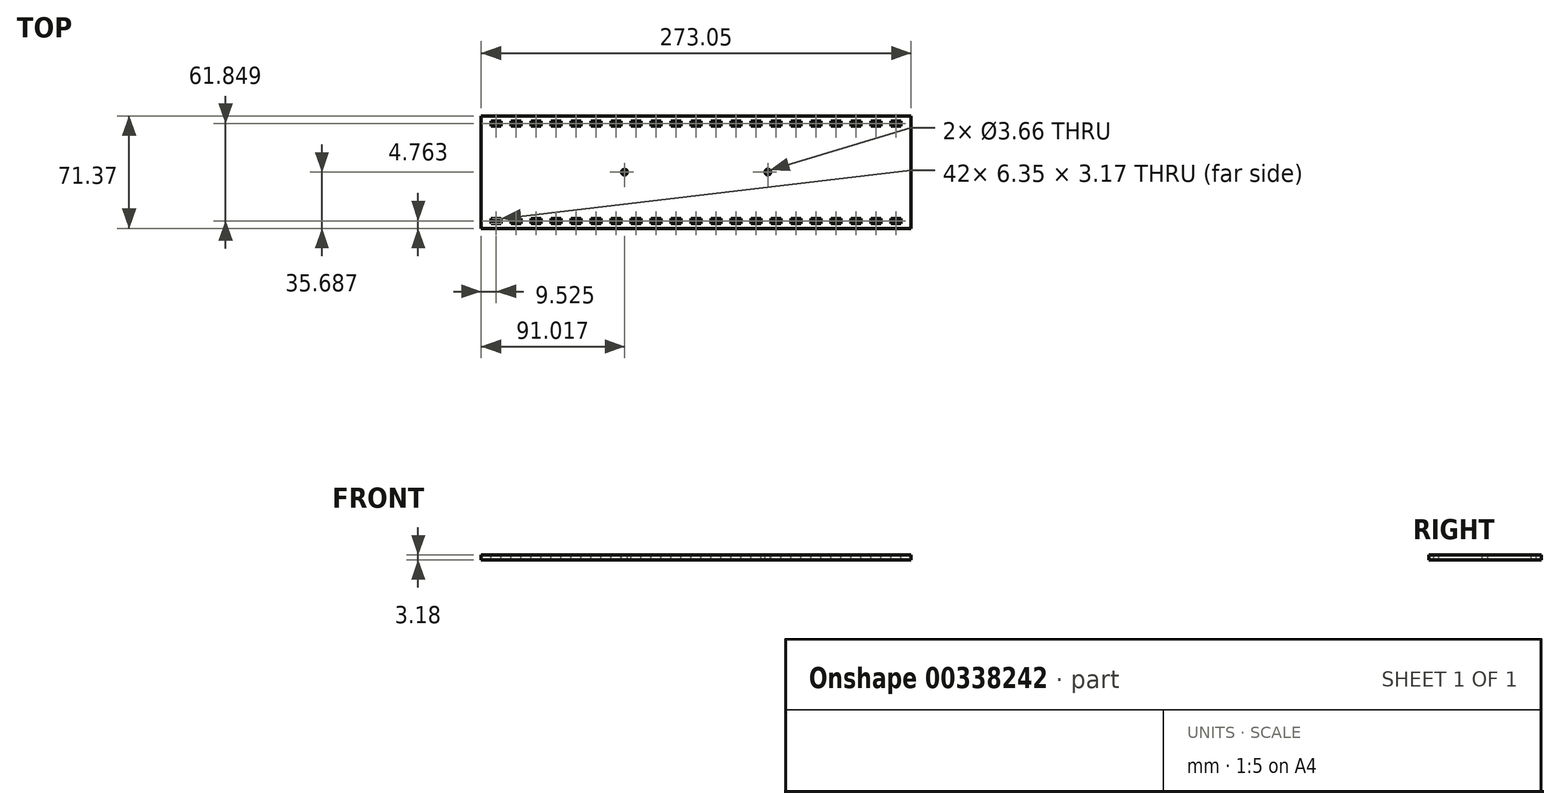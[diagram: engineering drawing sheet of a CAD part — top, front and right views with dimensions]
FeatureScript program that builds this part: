
annotation { "Feature Type Name" : "Feature", "Feature Type Description" : "" }
export const myFeature = defineFeature(function(context is Context, id is Id, definition is map)
    precondition{}
    {
        {
            var Q0;
            Q0=qCreatedBy(makeId("Top.planeOp"),FACE);
            var sketch = newSketch(context, id + "F0", { "sketchPlane" : qUnion([Q0])});
            skLineSegment(sketch, "E0.bottom", {"start": v(0, 0) * mm, "end": v(-273.05, 0) * mm});
            skLineSegment(sketch, "E0.top", {"start": v(0, 71.37) * mm, "end": v(-273.05, 71.37) * mm});
            skLineSegment(sketch, "E0.left", {"start": v(0, 0) * mm, "end": v(0, 71.37) * mm});
            skLineSegment(sketch, "E0.right", {"start": v(-273.05, 0) * mm, "end": v(-273.05, 71.37) * mm});
            skSolve(sketch);
        }
        {
            var Q0;
            Q0=qSketchRegion(id+"F0",true);
            extrude(context, id + "F1", {"entities" : qUnion([Q0]), "depth" : 3.17 * mm});
        }
        {
            var Q0;
            Q0=makeQuery(id+"F1.opExtrude","CAP_FACE",FACE,{"disambiguationData":[OSD([sQuery(id+"F0.wireOp",EDGE,"E0.bottom"),sQuery(id+"F0.wireOp",EDGE,"E0.top"),sQuery(id+"F0.wireOp",EDGE,"E0.left"),sQuery(id+"F0.wireOp",EDGE,"E0.right")])],"isStart":false});
            var sketch = newSketch(context, id + "F2", { "sketchPlane" : qUnion([Q0])});
            skLineSegment(sketch, "E1", {"start": v(0, 4.76) * mm, "end": v(-6.35, 4.76) * mm, "construction": true});
            skLineSegment(sketch, "E2", {"start": v(0, 35.69) * mm, "end": v(-91.02, 35.69) * mm, "construction": true});
            skLineSegment(sketch, "E3", {"start": v(-91.02, 35.69) * mm, "end": v(-182.03, 35.69) * mm, "construction": true});
            skLineSegment(sketch, "E4", {"start": v(-182.03, 35.69) * mm, "end": v(-273.05, 35.69) * mm, "construction": true});
            skCircle(sketch, "E5", {"center": v(-182.03, 35.69) * mm, "radius": 1.83 * mm});
            skCircle(sketch, "E6", {"center": v(-91.02, 35.69) * mm, "radius": 1.83 * mm});
            skLineSegment(sketch, "E7.bottom", {"start": v(-6.35, 3.18) * mm, "end": v(-12.7, 3.17) * mm});
            skLineSegment(sketch, "E7.top", {"start": v(-6.35, 6.35) * mm, "end": v(-12.7, 6.35) * mm});
            skLineSegment(sketch, "E7.left", {"start": v(-6.35, 3.17) * mm, "end": v(-6.35, 6.35) * mm});
            skLineSegment(sketch, "E7.right", {"start": v(-12.7, 3.18) * mm, "end": v(-12.7, 6.35) * mm});
            skLineSegment(sketch, "E8", {"start": v(-9.53, 3.18) * mm, "end": v(-9.53, 0) * mm, "construction": true});
            skLineSegment(sketch, "E9", {"start": v(-9.53, 71.37) * mm, "end": v(-9.53, 68.2) * mm, "construction": true});
            skLineSegment(sketch, "E10.bottom", {"start": v(-12.7, 68.2) * mm, "end": v(-6.35, 68.2) * mm});
            skLineSegment(sketch, "E10.top", {"start": v(-12.7, 65.02) * mm, "end": v(-6.35, 65.02) * mm});
            skLineSegment(sketch, "E10.left", {"start": v(-12.7, 68.2) * mm, "end": v(-12.7, 65.02) * mm});
            skLineSegment(sketch, "E10.right", {"start": v(-6.35, 68.2) * mm, "end": v(-6.35, 65.02) * mm});
            skLineSegment(sketch, "E11", {"start": v(-6.35, 66.61) * mm, "end": v(0, 66.61) * mm, "construction": true});
            skLineSegment(sketch, "E12.1.0.0", {"start": v(-19.05, 66.61) * mm, "end": v(-12.7, 66.61) * mm, "construction": true});
            skLineSegment(sketch, "E12.1.0.1", {"start": v(-25.4, 68.2) * mm, "end": v(-19.05, 68.2) * mm});
            skLineSegment(sketch, "E12.1.0.2", {"start": v(-25.4, 68.2) * mm, "end": v(-25.4, 65.02) * mm});
            skLineSegment(sketch, "E12.1.0.3", {"start": v(-25.4, 65.02) * mm, "end": v(-19.05, 65.02) * mm});
            skLineSegment(sketch, "E12.1.0.4", {"start": v(-19.05, 68.2) * mm, "end": v(-19.05, 65.02) * mm});
            skLineSegment(sketch, "E12.2.0.0", {"start": v(-31.75, 66.61) * mm, "end": v(-25.4, 66.61) * mm, "construction": true});
            skLineSegment(sketch, "E12.2.0.1", {"start": v(-38.1, 68.2) * mm, "end": v(-31.75, 68.2) * mm});
            skLineSegment(sketch, "E12.2.0.2", {"start": v(-38.1, 68.2) * mm, "end": v(-38.1, 65.02) * mm});
            skLineSegment(sketch, "E12.2.0.3", {"start": v(-38.1, 65.02) * mm, "end": v(-31.75, 65.02) * mm});
            skLineSegment(sketch, "E12.2.0.4", {"start": v(-31.75, 68.2) * mm, "end": v(-31.75, 65.02) * mm});
            skLineSegment(sketch, "E12.3.0.0", {"start": v(-44.45, 66.61) * mm, "end": v(-38.1, 66.61) * mm, "construction": true});
            skLineSegment(sketch, "E12.3.0.1", {"start": v(-50.8, 68.2) * mm, "end": v(-44.45, 68.2) * mm});
            skLineSegment(sketch, "E12.3.0.2", {"start": v(-50.8, 68.2) * mm, "end": v(-50.8, 65.02) * mm});
            skLineSegment(sketch, "E12.3.0.3", {"start": v(-50.8, 65.02) * mm, "end": v(-44.45, 65.02) * mm});
            skLineSegment(sketch, "E12.3.0.4", {"start": v(-44.45, 68.2) * mm, "end": v(-44.45, 65.02) * mm});
            skLineSegment(sketch, "E12.4.0.0", {"start": v(-57.15, 66.61) * mm, "end": v(-50.8, 66.61) * mm, "construction": true});
            skLineSegment(sketch, "E12.4.0.1", {"start": v(-63.5, 68.2) * mm, "end": v(-57.15, 68.2) * mm});
            skLineSegment(sketch, "E12.4.0.2", {"start": v(-63.5, 68.2) * mm, "end": v(-63.5, 65.02) * mm});
            skLineSegment(sketch, "E12.4.0.3", {"start": v(-63.5, 65.02) * mm, "end": v(-57.15, 65.02) * mm});
            skLineSegment(sketch, "E12.4.0.4", {"start": v(-57.15, 68.2) * mm, "end": v(-57.15, 65.02) * mm});
            skLineSegment(sketch, "E12.5.0.0", {"start": v(-69.85, 66.61) * mm, "end": v(-63.5, 66.61) * mm, "construction": true});
            skLineSegment(sketch, "E12.5.0.1", {"start": v(-76.2, 68.2) * mm, "end": v(-69.85, 68.2) * mm});
            skLineSegment(sketch, "E12.5.0.2", {"start": v(-76.2, 68.2) * mm, "end": v(-76.2, 65.02) * mm});
            skLineSegment(sketch, "E12.5.0.3", {"start": v(-76.2, 65.02) * mm, "end": v(-69.85, 65.02) * mm});
            skLineSegment(sketch, "E12.5.0.4", {"start": v(-69.85, 68.2) * mm, "end": v(-69.85, 65.02) * mm});
            skLineSegment(sketch, "E12.6.0.0", {"start": v(-82.55, 66.61) * mm, "end": v(-76.2, 66.61) * mm, "construction": true});
            skLineSegment(sketch, "E12.6.0.1", {"start": v(-88.9, 68.2) * mm, "end": v(-82.55, 68.2) * mm});
            skLineSegment(sketch, "E12.6.0.2", {"start": v(-88.9, 68.2) * mm, "end": v(-88.9, 65.02) * mm});
            skLineSegment(sketch, "E12.6.0.3", {"start": v(-88.9, 65.02) * mm, "end": v(-82.55, 65.02) * mm});
            skLineSegment(sketch, "E12.6.0.4", {"start": v(-82.55, 68.2) * mm, "end": v(-82.55, 65.02) * mm});
            skLineSegment(sketch, "E12.7.0.0", {"start": v(-95.25, 66.61) * mm, "end": v(-88.9, 66.61) * mm, "construction": true});
            skLineSegment(sketch, "E12.7.0.1", {"start": v(-101.6, 68.2) * mm, "end": v(-95.25, 68.2) * mm});
            skLineSegment(sketch, "E12.7.0.2", {"start": v(-101.6, 68.2) * mm, "end": v(-101.6, 65.02) * mm});
            skLineSegment(sketch, "E12.7.0.3", {"start": v(-101.6, 65.02) * mm, "end": v(-95.25, 65.02) * mm});
            skLineSegment(sketch, "E12.7.0.4", {"start": v(-95.25, 68.2) * mm, "end": v(-95.25, 65.02) * mm});
            skLineSegment(sketch, "E12.8.0.0", {"start": v(-107.95, 66.61) * mm, "end": v(-101.6, 66.61) * mm, "construction": true});
            skLineSegment(sketch, "E12.8.0.1", {"start": v(-114.3, 68.2) * mm, "end": v(-107.95, 68.2) * mm});
            skLineSegment(sketch, "E12.8.0.2", {"start": v(-114.3, 68.2) * mm, "end": v(-114.3, 65.02) * mm});
            skLineSegment(sketch, "E12.8.0.3", {"start": v(-114.3, 65.02) * mm, "end": v(-107.95, 65.02) * mm});
            skLineSegment(sketch, "E12.8.0.4", {"start": v(-107.95, 68.2) * mm, "end": v(-107.95, 65.02) * mm});
            skLineSegment(sketch, "E12.9.0.0", {"start": v(-120.65, 66.61) * mm, "end": v(-114.3, 66.61) * mm, "construction": true});
            skLineSegment(sketch, "E12.9.0.1", {"start": v(-127, 68.2) * mm, "end": v(-120.65, 68.2) * mm});
            skLineSegment(sketch, "E12.9.0.2", {"start": v(-127, 68.2) * mm, "end": v(-127, 65.02) * mm});
            skLineSegment(sketch, "E12.9.0.3", {"start": v(-127, 65.02) * mm, "end": v(-120.65, 65.02) * mm});
            skLineSegment(sketch, "E12.9.0.4", {"start": v(-120.65, 68.2) * mm, "end": v(-120.65, 65.02) * mm});
            skLineSegment(sketch, "E12.10.0.0", {"start": v(-133.35, 66.61) * mm, "end": v(-127, 66.61) * mm, "construction": true});
            skLineSegment(sketch, "E12.10.0.1", {"start": v(-139.7, 68.2) * mm, "end": v(-133.35, 68.2) * mm});
            skLineSegment(sketch, "E12.10.0.2", {"start": v(-139.7, 68.2) * mm, "end": v(-139.7, 65.02) * mm});
            skLineSegment(sketch, "E12.10.0.3", {"start": v(-139.7, 65.02) * mm, "end": v(-133.35, 65.02) * mm});
            skLineSegment(sketch, "E12.10.0.4", {"start": v(-133.35, 68.2) * mm, "end": v(-133.35, 65.02) * mm});
            skLineSegment(sketch, "E12.11.0.0", {"start": v(-146.05, 66.61) * mm, "end": v(-139.7, 66.61) * mm, "construction": true});
            skLineSegment(sketch, "E12.11.0.1", {"start": v(-152.4, 68.2) * mm, "end": v(-146.05, 68.2) * mm});
            skLineSegment(sketch, "E12.11.0.2", {"start": v(-152.4, 68.2) * mm, "end": v(-152.4, 65.02) * mm});
            skLineSegment(sketch, "E12.11.0.3", {"start": v(-152.4, 65.02) * mm, "end": v(-146.05, 65.02) * mm});
            skLineSegment(sketch, "E12.11.0.4", {"start": v(-146.05, 68.2) * mm, "end": v(-146.05, 65.02) * mm});
            skLineSegment(sketch, "E12.12.0.0", {"start": v(-158.75, 66.61) * mm, "end": v(-152.4, 66.61) * mm, "construction": true});
            skLineSegment(sketch, "E12.12.0.1", {"start": v(-165.1, 68.2) * mm, "end": v(-158.75, 68.2) * mm});
            skLineSegment(sketch, "E12.12.0.2", {"start": v(-165.1, 68.2) * mm, "end": v(-165.1, 65.02) * mm});
            skLineSegment(sketch, "E12.12.0.3", {"start": v(-165.1, 65.02) * mm, "end": v(-158.75, 65.02) * mm});
            skLineSegment(sketch, "E12.12.0.4", {"start": v(-158.75, 68.2) * mm, "end": v(-158.75, 65.02) * mm});
            skLineSegment(sketch, "E12.13.0.0", {"start": v(-171.45, 66.61) * mm, "end": v(-165.1, 66.61) * mm, "construction": true});
            skLineSegment(sketch, "E12.13.0.1", {"start": v(-177.8, 68.2) * mm, "end": v(-171.45, 68.2) * mm});
            skLineSegment(sketch, "E12.13.0.2", {"start": v(-177.8, 68.2) * mm, "end": v(-177.8, 65.02) * mm});
            skLineSegment(sketch, "E12.13.0.3", {"start": v(-177.8, 65.02) * mm, "end": v(-171.45, 65.02) * mm});
            skLineSegment(sketch, "E12.13.0.4", {"start": v(-171.45, 68.2) * mm, "end": v(-171.45, 65.02) * mm});
            skLineSegment(sketch, "E12.14.0.0", {"start": v(-184.15, 66.61) * mm, "end": v(-177.8, 66.61) * mm, "construction": true});
            skLineSegment(sketch, "E12.14.0.1", {"start": v(-190.5, 68.2) * mm, "end": v(-184.15, 68.2) * mm});
            skLineSegment(sketch, "E12.14.0.2", {"start": v(-190.5, 68.2) * mm, "end": v(-190.5, 65.02) * mm});
            skLineSegment(sketch, "E12.14.0.3", {"start": v(-190.5, 65.02) * mm, "end": v(-184.15, 65.02) * mm});
            skLineSegment(sketch, "E12.14.0.4", {"start": v(-184.15, 68.2) * mm, "end": v(-184.15, 65.02) * mm});
            skLineSegment(sketch, "E12.15.0.0", {"start": v(-196.85, 66.61) * mm, "end": v(-190.5, 66.61) * mm, "construction": true});
            skLineSegment(sketch, "E12.15.0.1", {"start": v(-203.2, 68.2) * mm, "end": v(-196.85, 68.2) * mm});
            skLineSegment(sketch, "E12.15.0.2", {"start": v(-203.2, 68.2) * mm, "end": v(-203.2, 65.02) * mm});
            skLineSegment(sketch, "E12.15.0.3", {"start": v(-203.2, 65.02) * mm, "end": v(-196.85, 65.02) * mm});
            skLineSegment(sketch, "E12.15.0.4", {"start": v(-196.85, 68.2) * mm, "end": v(-196.85, 65.02) * mm});
            skLineSegment(sketch, "E12.16.0.0", {"start": v(-209.55, 66.61) * mm, "end": v(-203.2, 66.61) * mm, "construction": true});
            skLineSegment(sketch, "E12.16.0.1", {"start": v(-215.9, 68.2) * mm, "end": v(-209.55, 68.2) * mm});
            skLineSegment(sketch, "E12.16.0.2", {"start": v(-215.9, 68.2) * mm, "end": v(-215.9, 65.02) * mm});
            skLineSegment(sketch, "E12.16.0.3", {"start": v(-215.9, 65.02) * mm, "end": v(-209.55, 65.02) * mm});
            skLineSegment(sketch, "E12.16.0.4", {"start": v(-209.55, 68.2) * mm, "end": v(-209.55, 65.02) * mm});
            skLineSegment(sketch, "E12.17.0.0", {"start": v(-222.25, 66.61) * mm, "end": v(-215.9, 66.61) * mm, "construction": true});
            skLineSegment(sketch, "E12.17.0.1", {"start": v(-228.6, 68.2) * mm, "end": v(-222.25, 68.2) * mm});
            skLineSegment(sketch, "E12.17.0.2", {"start": v(-228.6, 68.2) * mm, "end": v(-228.6, 65.02) * mm});
            skLineSegment(sketch, "E12.17.0.3", {"start": v(-228.6, 65.02) * mm, "end": v(-222.25, 65.02) * mm});
            skLineSegment(sketch, "E12.17.0.4", {"start": v(-222.25, 68.2) * mm, "end": v(-222.25, 65.02) * mm});
            skLineSegment(sketch, "E12.18.0.0", {"start": v(-234.95, 66.61) * mm, "end": v(-228.6, 66.61) * mm, "construction": true});
            skLineSegment(sketch, "E12.18.0.1", {"start": v(-241.3, 68.2) * mm, "end": v(-234.95, 68.2) * mm});
            skLineSegment(sketch, "E12.18.0.2", {"start": v(-241.3, 68.2) * mm, "end": v(-241.3, 65.02) * mm});
            skLineSegment(sketch, "E12.18.0.3", {"start": v(-241.3, 65.02) * mm, "end": v(-234.95, 65.02) * mm});
            skLineSegment(sketch, "E12.18.0.4", {"start": v(-234.95, 68.2) * mm, "end": v(-234.95, 65.02) * mm});
            skLineSegment(sketch, "E12.19.0.0", {"start": v(-247.65, 66.61) * mm, "end": v(-241.3, 66.61) * mm, "construction": true});
            skLineSegment(sketch, "E12.19.0.1", {"start": v(-254, 68.2) * mm, "end": v(-247.65, 68.2) * mm});
            skLineSegment(sketch, "E12.19.0.2", {"start": v(-254, 68.2) * mm, "end": v(-254, 65.02) * mm});
            skLineSegment(sketch, "E12.19.0.3", {"start": v(-254, 65.02) * mm, "end": v(-247.65, 65.02) * mm});
            skLineSegment(sketch, "E12.19.0.4", {"start": v(-247.65, 68.2) * mm, "end": v(-247.65, 65.02) * mm});
            skLineSegment(sketch, "E12.20.0.0", {"start": v(-260.35, 66.61) * mm, "end": v(-254, 66.61) * mm, "construction": true});
            skLineSegment(sketch, "E12.20.0.1", {"start": v(-266.7, 68.2) * mm, "end": v(-260.35, 68.2) * mm});
            skLineSegment(sketch, "E12.20.0.2", {"start": v(-266.7, 68.2) * mm, "end": v(-266.7, 65.02) * mm});
            skLineSegment(sketch, "E12.20.0.3", {"start": v(-266.7, 65.02) * mm, "end": v(-260.35, 65.02) * mm});
            skLineSegment(sketch, "E12.20.0.4", {"start": v(-260.35, 68.2) * mm, "end": v(-260.35, 65.02) * mm});
            skLineSegment(sketch, "E12.21.0.0", {"start": v(-273.05, 66.61) * mm, "end": v(-266.7, 66.61) * mm, "construction": true});
            skLineSegment(sketch, "E12.21.0.1", {"start": v(-279.4, 68.2) * mm, "end": v(-273.05, 68.2) * mm});
            skLineSegment(sketch, "E12.21.0.2", {"start": v(-279.4, 68.2) * mm, "end": v(-279.4, 65.02) * mm});
            skLineSegment(sketch, "E12.21.0.3", {"start": v(-279.4, 65.02) * mm, "end": v(-273.05, 65.02) * mm});
            skLineSegment(sketch, "E12.21.0.4", {"start": v(-273.05, 68.2) * mm, "end": v(-273.05, 65.02) * mm});
            skLineSegment(sketch, "E12.direction1", {"start": v(-12.7, 65.02) * mm, "end": v(-25.4, 65.02) * mm, "construction": true});
            skLineSegment(sketch, "E13.1.0.0", {"start": v(-12.7, 4.76) * mm, "end": v(-19.05, 4.76) * mm, "construction": true});
            skLineSegment(sketch, "E13.1.0.1", {"start": v(-19.05, 6.35) * mm, "end": v(-25.4, 6.35) * mm});
            skLineSegment(sketch, "E13.1.0.2", {"start": v(-19.05, 3.17) * mm, "end": v(-19.05, 6.35) * mm});
            skLineSegment(sketch, "E13.1.0.3", {"start": v(-25.4, 3.18) * mm, "end": v(-25.4, 6.35) * mm});
            skLineSegment(sketch, "E13.1.0.4", {"start": v(-19.05, 3.18) * mm, "end": v(-25.4, 3.17) * mm});
            skLineSegment(sketch, "E13.2.0.0", {"start": v(-25.4, 4.76) * mm, "end": v(-31.75, 4.76) * mm, "construction": true});
            skLineSegment(sketch, "E13.2.0.1", {"start": v(-31.75, 6.35) * mm, "end": v(-38.1, 6.35) * mm});
            skLineSegment(sketch, "E13.2.0.2", {"start": v(-31.75, 3.17) * mm, "end": v(-31.75, 6.35) * mm});
            skLineSegment(sketch, "E13.2.0.3", {"start": v(-38.1, 3.18) * mm, "end": v(-38.1, 6.35) * mm});
            skLineSegment(sketch, "E13.2.0.4", {"start": v(-31.75, 3.18) * mm, "end": v(-38.1, 3.17) * mm});
            skLineSegment(sketch, "E13.3.0.0", {"start": v(-38.1, 4.76) * mm, "end": v(-44.45, 4.76) * mm, "construction": true});
            skLineSegment(sketch, "E13.3.0.1", {"start": v(-44.45, 6.35) * mm, "end": v(-50.8, 6.35) * mm});
            skLineSegment(sketch, "E13.3.0.2", {"start": v(-44.45, 3.17) * mm, "end": v(-44.45, 6.35) * mm});
            skLineSegment(sketch, "E13.3.0.3", {"start": v(-50.8, 3.18) * mm, "end": v(-50.8, 6.35) * mm});
            skLineSegment(sketch, "E13.3.0.4", {"start": v(-44.45, 3.18) * mm, "end": v(-50.8, 3.17) * mm});
            skLineSegment(sketch, "E13.4.0.0", {"start": v(-50.8, 4.76) * mm, "end": v(-57.15, 4.76) * mm, "construction": true});
            skLineSegment(sketch, "E13.4.0.1", {"start": v(-57.15, 6.35) * mm, "end": v(-63.5, 6.35) * mm});
            skLineSegment(sketch, "E13.4.0.2", {"start": v(-57.15, 3.17) * mm, "end": v(-57.15, 6.35) * mm});
            skLineSegment(sketch, "E13.4.0.3", {"start": v(-63.5, 3.18) * mm, "end": v(-63.5, 6.35) * mm});
            skLineSegment(sketch, "E13.4.0.4", {"start": v(-57.15, 3.18) * mm, "end": v(-63.5, 3.17) * mm});
            skLineSegment(sketch, "E13.5.0.0", {"start": v(-63.5, 4.76) * mm, "end": v(-69.85, 4.76) * mm, "construction": true});
            skLineSegment(sketch, "E13.5.0.1", {"start": v(-69.85, 6.35) * mm, "end": v(-76.2, 6.35) * mm});
            skLineSegment(sketch, "E13.5.0.2", {"start": v(-69.85, 3.17) * mm, "end": v(-69.85, 6.35) * mm});
            skLineSegment(sketch, "E13.5.0.3", {"start": v(-76.2, 3.18) * mm, "end": v(-76.2, 6.35) * mm});
            skLineSegment(sketch, "E13.5.0.4", {"start": v(-69.85, 3.18) * mm, "end": v(-76.2, 3.17) * mm});
            skLineSegment(sketch, "E13.6.0.0", {"start": v(-76.2, 4.76) * mm, "end": v(-82.55, 4.76) * mm, "construction": true});
            skLineSegment(sketch, "E13.6.0.1", {"start": v(-82.55, 6.35) * mm, "end": v(-88.9, 6.35) * mm});
            skLineSegment(sketch, "E13.6.0.2", {"start": v(-82.55, 3.17) * mm, "end": v(-82.55, 6.35) * mm});
            skLineSegment(sketch, "E13.6.0.3", {"start": v(-88.9, 3.18) * mm, "end": v(-88.9, 6.35) * mm});
            skLineSegment(sketch, "E13.6.0.4", {"start": v(-82.55, 3.18) * mm, "end": v(-88.9, 3.17) * mm});
            skLineSegment(sketch, "E13.7.0.0", {"start": v(-88.9, 4.76) * mm, "end": v(-95.25, 4.76) * mm, "construction": true});
            skLineSegment(sketch, "E13.7.0.1", {"start": v(-95.25, 6.35) * mm, "end": v(-101.6, 6.35) * mm});
            skLineSegment(sketch, "E13.7.0.2", {"start": v(-95.25, 3.17) * mm, "end": v(-95.25, 6.35) * mm});
            skLineSegment(sketch, "E13.7.0.3", {"start": v(-101.6, 3.18) * mm, "end": v(-101.6, 6.35) * mm});
            skLineSegment(sketch, "E13.7.0.4", {"start": v(-95.25, 3.18) * mm, "end": v(-101.6, 3.17) * mm});
            skLineSegment(sketch, "E13.8.0.0", {"start": v(-101.6, 4.76) * mm, "end": v(-107.95, 4.76) * mm, "construction": true});
            skLineSegment(sketch, "E13.8.0.1", {"start": v(-107.95, 6.35) * mm, "end": v(-114.3, 6.35) * mm});
            skLineSegment(sketch, "E13.8.0.2", {"start": v(-107.95, 3.17) * mm, "end": v(-107.95, 6.35) * mm});
            skLineSegment(sketch, "E13.8.0.3", {"start": v(-114.3, 3.18) * mm, "end": v(-114.3, 6.35) * mm});
            skLineSegment(sketch, "E13.8.0.4", {"start": v(-107.95, 3.18) * mm, "end": v(-114.3, 3.17) * mm});
            skLineSegment(sketch, "E13.9.0.0", {"start": v(-114.3, 4.76) * mm, "end": v(-120.65, 4.76) * mm, "construction": true});
            skLineSegment(sketch, "E13.9.0.1", {"start": v(-120.65, 6.35) * mm, "end": v(-127, 6.35) * mm});
            skLineSegment(sketch, "E13.9.0.2", {"start": v(-120.65, 3.17) * mm, "end": v(-120.65, 6.35) * mm});
            skLineSegment(sketch, "E13.9.0.3", {"start": v(-127, 3.18) * mm, "end": v(-127, 6.35) * mm});
            skLineSegment(sketch, "E13.9.0.4", {"start": v(-120.65, 3.18) * mm, "end": v(-127, 3.17) * mm});
            skLineSegment(sketch, "E13.10.0.0", {"start": v(-127, 4.76) * mm, "end": v(-133.35, 4.76) * mm, "construction": true});
            skLineSegment(sketch, "E13.10.0.1", {"start": v(-133.35, 6.35) * mm, "end": v(-139.7, 6.35) * mm});
            skLineSegment(sketch, "E13.10.0.2", {"start": v(-133.35, 3.17) * mm, "end": v(-133.35, 6.35) * mm});
            skLineSegment(sketch, "E13.10.0.3", {"start": v(-139.7, 3.18) * mm, "end": v(-139.7, 6.35) * mm});
            skLineSegment(sketch, "E13.10.0.4", {"start": v(-133.35, 3.18) * mm, "end": v(-139.7, 3.17) * mm});
            skLineSegment(sketch, "E13.11.0.0", {"start": v(-139.7, 4.76) * mm, "end": v(-146.05, 4.76) * mm, "construction": true});
            skLineSegment(sketch, "E13.11.0.1", {"start": v(-146.05, 6.35) * mm, "end": v(-152.4, 6.35) * mm});
            skLineSegment(sketch, "E13.11.0.2", {"start": v(-146.05, 3.17) * mm, "end": v(-146.05, 6.35) * mm});
            skLineSegment(sketch, "E13.11.0.3", {"start": v(-152.4, 3.18) * mm, "end": v(-152.4, 6.35) * mm});
            skLineSegment(sketch, "E13.11.0.4", {"start": v(-146.05, 3.18) * mm, "end": v(-152.4, 3.17) * mm});
            skLineSegment(sketch, "E13.12.0.0", {"start": v(-152.4, 4.76) * mm, "end": v(-158.75, 4.76) * mm, "construction": true});
            skLineSegment(sketch, "E13.12.0.1", {"start": v(-158.75, 6.35) * mm, "end": v(-165.1, 6.35) * mm});
            skLineSegment(sketch, "E13.12.0.2", {"start": v(-158.75, 3.17) * mm, "end": v(-158.75, 6.35) * mm});
            skLineSegment(sketch, "E13.12.0.3", {"start": v(-165.1, 3.18) * mm, "end": v(-165.1, 6.35) * mm});
            skLineSegment(sketch, "E13.12.0.4", {"start": v(-158.75, 3.18) * mm, "end": v(-165.1, 3.17) * mm});
            skLineSegment(sketch, "E13.13.0.0", {"start": v(-165.1, 4.76) * mm, "end": v(-171.45, 4.76) * mm, "construction": true});
            skLineSegment(sketch, "E13.13.0.1", {"start": v(-171.45, 6.35) * mm, "end": v(-177.8, 6.35) * mm});
            skLineSegment(sketch, "E13.13.0.2", {"start": v(-171.45, 3.17) * mm, "end": v(-171.45, 6.35) * mm});
            skLineSegment(sketch, "E13.13.0.3", {"start": v(-177.8, 3.18) * mm, "end": v(-177.8, 6.35) * mm});
            skLineSegment(sketch, "E13.13.0.4", {"start": v(-171.45, 3.18) * mm, "end": v(-177.8, 3.17) * mm});
            skLineSegment(sketch, "E13.14.0.0", {"start": v(-177.8, 4.76) * mm, "end": v(-184.15, 4.76) * mm, "construction": true});
            skLineSegment(sketch, "E13.14.0.1", {"start": v(-184.15, 6.35) * mm, "end": v(-190.5, 6.35) * mm});
            skLineSegment(sketch, "E13.14.0.2", {"start": v(-184.15, 3.17) * mm, "end": v(-184.15, 6.35) * mm});
            skLineSegment(sketch, "E13.14.0.3", {"start": v(-190.5, 3.18) * mm, "end": v(-190.5, 6.35) * mm});
            skLineSegment(sketch, "E13.14.0.4", {"start": v(-184.15, 3.18) * mm, "end": v(-190.5, 3.17) * mm});
            skLineSegment(sketch, "E13.15.0.0", {"start": v(-190.5, 4.76) * mm, "end": v(-196.85, 4.76) * mm, "construction": true});
            skLineSegment(sketch, "E13.15.0.1", {"start": v(-196.85, 6.35) * mm, "end": v(-203.2, 6.35) * mm});
            skLineSegment(sketch, "E13.15.0.2", {"start": v(-196.85, 3.17) * mm, "end": v(-196.85, 6.35) * mm});
            skLineSegment(sketch, "E13.15.0.3", {"start": v(-203.2, 3.18) * mm, "end": v(-203.2, 6.35) * mm});
            skLineSegment(sketch, "E13.15.0.4", {"start": v(-196.85, 3.18) * mm, "end": v(-203.2, 3.17) * mm});
            skLineSegment(sketch, "E13.16.0.0", {"start": v(-203.2, 4.76) * mm, "end": v(-209.55, 4.76) * mm, "construction": true});
            skLineSegment(sketch, "E13.16.0.1", {"start": v(-209.55, 6.35) * mm, "end": v(-215.9, 6.35) * mm});
            skLineSegment(sketch, "E13.16.0.2", {"start": v(-209.55, 3.17) * mm, "end": v(-209.55, 6.35) * mm});
            skLineSegment(sketch, "E13.16.0.3", {"start": v(-215.9, 3.18) * mm, "end": v(-215.9, 6.35) * mm});
            skLineSegment(sketch, "E13.16.0.4", {"start": v(-209.55, 3.18) * mm, "end": v(-215.9, 3.17) * mm});
            skLineSegment(sketch, "E13.17.0.0", {"start": v(-215.9, 4.76) * mm, "end": v(-222.25, 4.76) * mm, "construction": true});
            skLineSegment(sketch, "E13.17.0.1", {"start": v(-222.25, 6.35) * mm, "end": v(-228.6, 6.35) * mm});
            skLineSegment(sketch, "E13.17.0.2", {"start": v(-222.25, 3.17) * mm, "end": v(-222.25, 6.35) * mm});
            skLineSegment(sketch, "E13.17.0.3", {"start": v(-228.6, 3.18) * mm, "end": v(-228.6, 6.35) * mm});
            skLineSegment(sketch, "E13.17.0.4", {"start": v(-222.25, 3.18) * mm, "end": v(-228.6, 3.17) * mm});
            skLineSegment(sketch, "E13.18.0.0", {"start": v(-228.6, 4.76) * mm, "end": v(-234.95, 4.76) * mm, "construction": true});
            skLineSegment(sketch, "E13.18.0.1", {"start": v(-234.95, 6.35) * mm, "end": v(-241.3, 6.35) * mm});
            skLineSegment(sketch, "E13.18.0.2", {"start": v(-234.95, 3.17) * mm, "end": v(-234.95, 6.35) * mm});
            skLineSegment(sketch, "E13.18.0.3", {"start": v(-241.3, 3.18) * mm, "end": v(-241.3, 6.35) * mm});
            skLineSegment(sketch, "E13.18.0.4", {"start": v(-234.95, 3.18) * mm, "end": v(-241.3, 3.17) * mm});
            skLineSegment(sketch, "E13.19.0.0", {"start": v(-241.3, 4.76) * mm, "end": v(-247.65, 4.76) * mm, "construction": true});
            skLineSegment(sketch, "E13.19.0.1", {"start": v(-247.65, 6.35) * mm, "end": v(-254, 6.35) * mm});
            skLineSegment(sketch, "E13.19.0.2", {"start": v(-247.65, 3.17) * mm, "end": v(-247.65, 6.35) * mm});
            skLineSegment(sketch, "E13.19.0.3", {"start": v(-254, 3.18) * mm, "end": v(-254, 6.35) * mm});
            skLineSegment(sketch, "E13.19.0.4", {"start": v(-247.65, 3.18) * mm, "end": v(-254, 3.17) * mm});
            skLineSegment(sketch, "E13.20.0.0", {"start": v(-254, 4.76) * mm, "end": v(-260.35, 4.76) * mm, "construction": true});
            skLineSegment(sketch, "E13.20.0.1", {"start": v(-260.35, 6.35) * mm, "end": v(-266.7, 6.35) * mm});
            skLineSegment(sketch, "E13.20.0.2", {"start": v(-260.35, 3.17) * mm, "end": v(-260.35, 6.35) * mm});
            skLineSegment(sketch, "E13.20.0.3", {"start": v(-266.7, 3.18) * mm, "end": v(-266.7, 6.35) * mm});
            skLineSegment(sketch, "E13.20.0.4", {"start": v(-260.35, 3.18) * mm, "end": v(-266.7, 3.17) * mm});
            skLineSegment(sketch, "E13.21.0.0", {"start": v(-266.7, 4.76) * mm, "end": v(-273.05, 4.76) * mm, "construction": true});
            skLineSegment(sketch, "E13.21.0.1", {"start": v(-273.05, 6.35) * mm, "end": v(-279.4, 6.35) * mm});
            skLineSegment(sketch, "E13.21.0.2", {"start": v(-273.05, 3.17) * mm, "end": v(-273.05, 6.35) * mm});
            skLineSegment(sketch, "E13.21.0.3", {"start": v(-279.4, 3.18) * mm, "end": v(-279.4, 6.35) * mm});
            skLineSegment(sketch, "E13.21.0.4", {"start": v(-273.05, 3.18) * mm, "end": v(-279.4, 3.17) * mm});
            skLineSegment(sketch, "E13.direction1", {"start": v(-12.7, 3.17) * mm, "end": v(-25.4, 3.17) * mm, "construction": true});
            skSolve(sketch);
        }
        {
            var Q0;
            Q0=qSketchRegion(id+"F2",true);
            var Q1;
            Q1=makeQuery(id+"F1.opExtrude","CAP_FACE",FACE,{"disambiguationData":[OSD([sQuery(id+"F0.wireOp",EDGE,"E0.bottom"),sQuery(id+"F0.wireOp",EDGE,"E0.top"),sQuery(id+"F0.wireOp",EDGE,"E0.left"),sQuery(id+"F0.wireOp",EDGE,"E0.right")])],"isStart":true});
            extrude(context, id + "F3", {"entities" : qUnion([Q0]), "operationType" : NewBodyOperationType.REMOVE, "endBound" : BoundingType.UP_TO_SURFACE, "oppositeDirection" : true, "endBoundEntityFace" : qUnion([Q1]), "depth" : 25.4 * mm});
        }
    });
